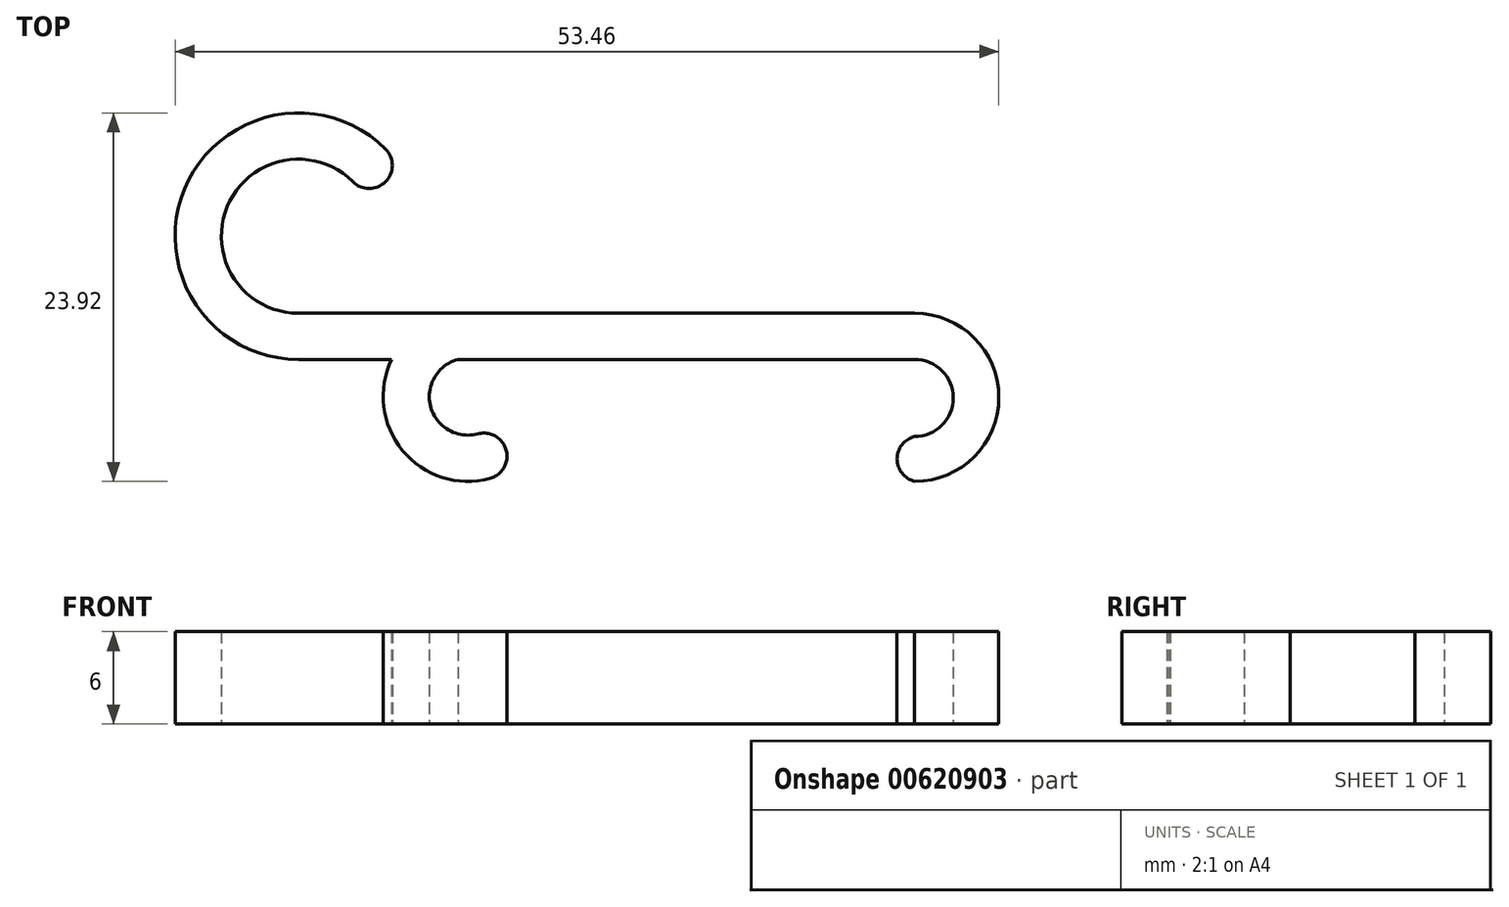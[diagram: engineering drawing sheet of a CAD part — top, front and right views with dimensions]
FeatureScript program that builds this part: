
annotation { "Feature Type Name" : "Feature", "Feature Type Description" : "" }
export const myFeature = defineFeature(function(context is Context, id is Id, definition is map)
    precondition{}
    {
        {
            var Q0;
            Q0=qCreatedBy(makeId("Top.planeOp"),FACE);
            var sketch = newSketch(context, id + "F0", { "sketchPlane" : qUnion([Q0])});
            skLineSegment(sketch, "E0", {"start": v(40, 0) * mm, "end": v(0, 0) * mm});
            skArc(sketch, "E1", {"start": v(0, 0) * mm, "mid": v(-4.62, 6.91) * mm, "end": v(3.54, 8.54) * mm});
            skArc(sketch, "E2.0", {"start": v(0, -3) * mm, "mid": v(-7.4, 8.06) * mm, "end": v(5.66, 10.66) * mm});
            skLineSegment(sketch, "E2.1", {"start": v(40, -3) * mm, "end": v(0, -3) * mm});
            skArc(sketch, "E3", {"start": v(40, -3) * mm, "mid": v(42.5, -5.5) * mm, "end": v(40, -8) * mm});
            skArc(sketch, "E4.0", {"start": v(40, 0) * mm, "mid": v(45.46, -5.46) * mm, "end": v(40, -10.92) * mm});
            skLineSegment(sketch, "E5", {"start": v(0, 0) * mm, "end": v(0, 5) * mm, "construction": true});
            skLineSegment(sketch, "E6", {"start": v(0, 5) * mm, "end": v(7.9, 12.9) * mm, "construction": true});
            skArc(sketch, "E7", {"start": v(5.66, 10.66) * mm, "mid": v(5.66, 8.54) * mm, "end": v(3.54, 8.54) * mm});
            skArc(sketch, "E8", {"start": v(10.35, -3) * mm, "mid": v(8.59, -6.06) * mm, "end": v(11.65, -7.83) * mm});
            skArc(sketch, "E9", {"start": v(11.65, -7.83) * mm, "mid": v(13.48, -8.9) * mm, "end": v(12.42, -10.73) * mm});
            skLineSegment(sketch, "E10", {"start": v(10.35, -3) * mm, "end": v(11.65, -7.83) * mm, "construction": true});
            skLineSegment(sketch, "E11", {"start": v(11.65, -7.83) * mm, "end": v(14.05, -16.8) * mm, "construction": true});
            skArc(sketch, "E12", {"start": v(12.42, -10.73) * mm, "mid": v(5.63, -6.6) * mm, "end": v(10.04, 0) * mm});
            skLineSegment(sketch, "E13", {"start": v(40, -3) * mm, "end": v(40, -14.22) * mm, "construction": true});
            skArc(sketch, "E14", {"start": v(40, -8) * mm, "mid": v(38.86, -9.46) * mm, "end": v(40, -10.92) * mm});
            skLineSegment(sketch, "E15", {"start": v(10.35, -3) * mm, "end": v(10.35, -20.07) * mm, "construction": true});
            skLineSegment(sketch, "E16", {"start": v(40, -3) * mm, "end": v(40, -18.53) * mm, "construction": true});
            skSolve(sketch);
        }
        {
            var Q0;
            Q0 = qSketchRegion(id + "F0", true);
            extrude(context, id + "F1", {"entities" : qUnion([Q0]), "depth" : 6 * mm, "offsetDistance" : 25 * mm});
        }
    });
